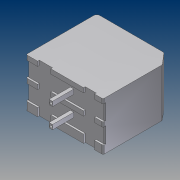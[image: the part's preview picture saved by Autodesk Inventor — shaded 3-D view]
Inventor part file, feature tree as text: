
AUTODESK INVENTOR PART (.ipt)
format: ipt  version: 2012 (Build 160160000, 160)  size: 281,600 bytes
history: native  units: mm (DEFAULTED — no unit token found)
features: sketch x20, extrude x19, pattern_linear x9, revolve x1
ambient origin geometry x8: Origin, YZ Plane, XZ Plane, XY Plane, X Axis, Y Axis, Z Axis, Center Point
bodies: Solid1 (feature_tree)
feature tree (49):
  extrude  "Extrusion1"  Depth=0.8mm TaperAngle=0.0deg
  extrude  "Extrusion2"  Depth=0.8mm TaperAngle=0.0deg
  pattern_linear  "Rectangular Pattern1"  Count1=2 Spacing1=3.5mm
  extrude  "Extrusion3"  Depth=20.0mm TaperAngle=0.0deg
  pattern_linear  "Rectangular Pattern2"  Count1=2 Spacing1=3.5mm
  extrude  "Extrusion4"  Depth=20.0mm TaperAngle=0.0deg
  pattern_linear  "Rectangular Pattern3"  Count1=2 Spacing1=3.5mm
  extrude  "Extrusion5"  TaperAngle=360.0deg  [1 undecoded]
  extrude  "Extrusion6"  Depth=1.0mm TaperAngle=0.0deg
  extrude  "Extrusion7"  Depth=3.7mm TaperAngle=0.0deg
  extrude  "Extrusion8"  Depth=0.5mm
  extrude  "Extrusion9"  [1 undecoded]
  extrude  "Extrusion10"  [1 undecoded]
  extrude  "Extrusion11"  [1 undecoded]
  extrude  "Extrusion12"  [1 undecoded]
  extrude  "Extrusion13"  [1 undecoded]
  pattern_linear  "Rectangular Pattern4"  [2 undecoded]
  extrude  "Extrusion14"  [1 undecoded]
  pattern_linear  "Rectangular Pattern5"  [2 undecoded]
  extrude  "Extrusion15"  [1 undecoded]
  pattern_linear  "Rectangular Pattern6"  [2 undecoded]
  extrude  "Extrusion16"  [1 undecoded]
  revolve  "Revolution1"  [1 undecoded]
  pattern_linear  "Rectangular Pattern7"  [2 undecoded]
  extrude  "Extrusion17"  [1 undecoded]
  pattern_linear  "Rectangular Pattern8"  [2 undecoded]
  extrude  "Extrusion18"  [1 undecoded]
  pattern_linear  "Rectangular Pattern9"  [2 undecoded]
  extrude  "Extrusion19"  [1 undecoded]
  sketch  "Skizze_1"  dims[d0=7.0mm d1=0.0mm d2=0.8mm d3=0.0mm]
  sketch  "Skizze_2"  dims[d4=20.0mm d6=3.5mm d7=10.0mm d9=0.0mm d10=0.8mm d11=0.0mm d12=20.0mm d14=3.5mm d15=10.0mm d17=0.0mm]
  sketch  "Skizze_4"  dims[d18=0.8mm d19=0.0mm d20=20.0mm d22=3.5mm d23=10.0mm d25=0.0mm]
  sketch  "Skizze_6"  dims[d26=1.5mm d27=0.0mm]
  sketch  "Skizze_8"  dims[d28=1.5mm d29=0.0mm]
  sketch  "Skizze_9"  dims[d30=1.5mm d31=0.0mm]
  sketch  "Skizze_10"  dims[d32=1.5mm d33=0.0mm]
  sketch  "Skizze_11"  dims[d34=1.5mm d35=0.0mm]
  sketch  "Skizze_12"  dims[d36=1.5mm d37=0.0mm]
  sketch  "Skizze_13"  dims[d38=1.5mm d39=0.0mm]
  sketch  "Skizze_14"  dims[d40=1.4mm d41=0.0mm]
  sketch  "Skizze_15"  dims[d42=3.2mm d43=0.0mm d44=20.0mm d46=3.5mm d47=10.0mm d49=0.0mm]
  sketch  "Skizze_16"  dims[d50=6.0mm d51=0.0mm d52=20.0mm d54=3.5mm d55=10.0mm d57=0.0mm]
  sketch  "Skizze_18"  dims[d58=4.1mm d59=0.0mm d60=20.0mm d62=3.5mm d63=10.0mm d65=0.0mm]
  sketch  "Skizze_20"  dims[d66=7.0mm d67=0.0mm d68=360.0deg]
  sketch  "Skizze_22"  dims[d77=20.0mm d79=3.5mm d80=10.0mm d82=0.0mm d83=3.7mm d84=0.0mm]
  sketch  "Skizze_23"  dims[d85=20.0mm d87=3.5mm d88=10.0mm d90=0.0mm d91=0.5mm]
  sketch  "Skizze_24"  dims[d92=0.5mm d93=0.0mm]
  sketch  "Skizze_27"
  sketch  "Sketch20"  dims[d69=20.0mm d71=3.5mm d72=10.0mm d74=0.0mm d75=1.0mm d76=0.0mm]
note: 25 required parameter values undecoded (feature->parameter linkage not recoverable at this tier; creation-order binding heuristic only, values carry confidence <= 0.55)
